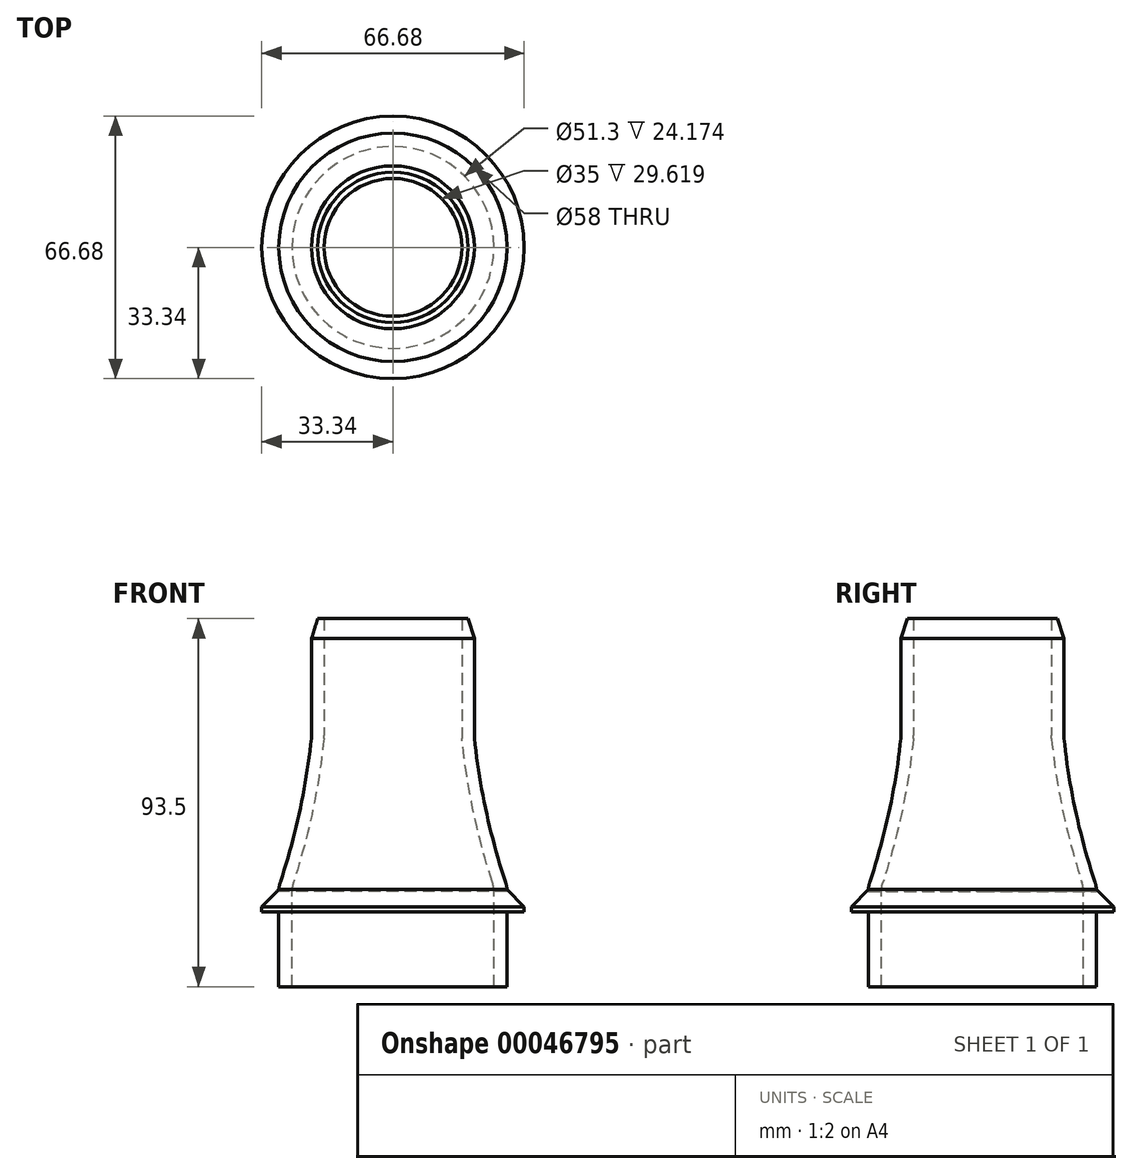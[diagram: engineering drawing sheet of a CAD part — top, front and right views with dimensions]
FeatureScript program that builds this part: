
annotation { "Feature Type Name" : "Feature", "Feature Type Description" : "" }
export const myFeature = defineFeature(function(context is Context, id is Id, definition is map)
    precondition{}
    {
        {
            var Q0;
            Q0=qCreatedBy(makeId("Front.planeOp"),FACE);
            var sketch = newSketch(context, id + "F0", { "sketchPlane" : qUnion([Q0])});
            skLineSegment(sketch, "E0", {"start": v(0, 0) * mm, "end": v(0, 38.1) * mm});
            skLineSegment(sketch, "E1", {"start": v(17.5, 38.1) * mm, "end": v(20.7, 38.1) * mm});
            skLineSegment(sketch, "E2", {"start": v(25.65, 0) * mm, "end": v(29, 0) * mm});
            skArc(sketch, "E3", {"start": v(20.7, 38.1) * mm, "mid": v(23.76, 18.81) * mm, "end": v(29, 0) * mm});
            skArc(sketch, "E4.0", {"start": v(17.5, 38.1) * mm, "mid": v(20.5, 18.82) * mm, "end": v(25.65, 0) * mm});
            skSolve(sketch);
        }
        {
            var Q0;
            Q0 = qSketchRegion(id + "F0", true);
            var Q1;
            Q1=sQuery(id+"F0.wireOp",EDGE,"E0");
            revolve(context, id + "F1", {"entities" : qUnion([Q0]), "axis" : qUnion([Q1]), "revolveType" : RevolveType.FULL});
        }
        {
            var Q0;
            Q0=makeQuery(id+"F1.opRevolve","SWEPT_FACE",FACE,{"disambiguationData":[OSD([sQuery(id+"F0.wireOp",EDGE,"E2")])]});
            var sketch = newSketch(context, id + "F2", { "sketchPlane" : qUnion([Q0])});
            skCircle(sketch, "E5", {"center": v(0, 0) * mm, "radius": 33.34 * mm});
            skCircle(sketch, "E6", {"center": v(0, 0) * mm, "radius": 25.4 * mm});
            skSolve(sketch);
        }
        {
            var Q0;
            Q0=makeQuery(id+"F1.opRevolve","SWEPT_FACE",FACE,{"disambiguationData":[OSD([sQuery(id+"F0.wireOp",EDGE,"E2")])]});
            extrude(context, id + "F3", {"entities" : qUnion([Q0]), "operationType" : NewBodyOperationType.ADD, "depth" : 25.4 * mm, "offsetDistance" : 25.4 * mm});
        }
        {
            var Q0;
            Q0=makeQuery(id+"F1.opRevolve","SWEPT_FACE",FACE,{"disambiguationData":[OSD([sQuery(id+"F0.wireOp",EDGE,"E1")])]});
            extrude(context, id + "F4", {"entities" : qUnion([Q0]), "operationType" : NewBodyOperationType.ADD, "depth" : 30 * mm});
        }
        {
            var Q0;
            {var subQ0=sQuery(id+"F0.wireOp",EDGE,"E2");var subQ1=sQuery(id+"F0.wireOp",EDGE,"E3");Q0=makeQuery(id+"F3.boolean.opBoolean","MERGE",EDGE,{"derivedFrom":[makeQuery(id+"F1.opRevolve","SWEPT_EDGE",EDGE,{"disambiguationData":[OSD([subQ0,subQ1])]}),makeQuery(id+"F3.opExtrude","CAP_EDGE",EDGE,{"disambiguationData":[OSD([subQ0,subQ1])],"isStart":true})]});}
            var Q1;
            {var subQ0=sQuery(id+"F0.wireOp",EDGE,"E1");var subQ1=sQuery(id+"F0.wireOp",EDGE,"E3");Q1=makeQuery(id+"F4.boolean.opBoolean","MERGE",EDGE,{"derivedFrom":[makeQuery(id+"F1.opRevolve","SWEPT_EDGE",EDGE,{"disambiguationData":[OSD([subQ0,subQ1])]}),makeQuery(id+"F4.opExtrude","CAP_EDGE",EDGE,{"disambiguationData":[OSD([subQ0,subQ1])],"isStart":true})]});}
            var Q2;
            {var subQ0=sQuery(id+"F0.wireOp",EDGE,"E2");var subQ1=sQuery(id+"F0.wireOp",EDGE,"E4.0");Q2=makeQuery(id+"F3.boolean.opBoolean","MERGE",EDGE,{"derivedFrom":[makeQuery(id+"F1.opRevolve","SWEPT_EDGE",EDGE,{"disambiguationData":[OSD([subQ0,subQ1])]}),makeQuery(id+"F3.opExtrude","CAP_EDGE",EDGE,{"disambiguationData":[OSD([subQ0,subQ1])],"isStart":true})]});}
            var Q3;
            {var subQ0=sQuery(id+"F0.wireOp",EDGE,"E1");var subQ1=sQuery(id+"F0.wireOp",EDGE,"E4.0");Q3=makeQuery(id+"F4.boolean.opBoolean","MERGE",EDGE,{"derivedFrom":[makeQuery(id+"F1.opRevolve","SWEPT_EDGE",EDGE,{"disambiguationData":[OSD([subQ0,subQ1])]}),makeQuery(id+"F4.opExtrude","CAP_EDGE",EDGE,{"disambiguationData":[OSD([subQ0,subQ1])],"isStart":true})]});}
            fillet(context, id + "F5", {"entities" : qUnion([Q0, Q1, Q2, Q3]), "radius" : 7.62 * mm, "tangentPropagation" : true, "allowEdgeOverflow" : false});
        }
        {
            var Q0;
            Q0=makeQuery(id+"F4.opExtrude","CAP_EDGE",EDGE,{"disambiguationData":[OSD([sQuery(id+"F0.wireOp",EDGE,"E1"),sQuery(id+"F0.wireOp",EDGE,"E3")])],"isStart":false});
            chamfer(context, id + "F6", {"entities" : qUnion([Q0]), "chamferType" : ChamferType.TWO_OFFSETS, "width1" : 1.59 * mm, "oppositeDirection" : true, "width2" : 5.08 * mm, "tangentPropagation" : true});
        }
        {
            var Q0;
            Q0=makeQuery(id+"F2.imprint","IMPRINT",FACE,{"disambiguationData":[TD([[makeQuery(id+"F2.imprint","IMPRINT",EDGE,{"derivedFrom":sQuery(id+"F2.wireOp",EDGE,"E5")}),1.0]])]});
            extrude(context, id + "F7", {"entities" : qUnion([Q0]), "operationType" : NewBodyOperationType.ADD, "depth" : 6.35 * mm, "offsetDistance" : 25.4 * mm});
        }
        {
            var Q0;
            Q0=makeQuery(id+"F7.opExtrude","CAP_EDGE",EDGE,{"disambiguationData":[OSD([sQuery(id+"F2.wireOp",EDGE,"E5")])],"isStart":true});
            chamfer(context, id + "F8", {"entities" : qUnion([Q0]), "width" : 5.08 * mm, "tangentPropagation" : true});
        }
    });
